# Revit family: Light_Fixture-Wall_Sconce-KOHLER-PURIST-K-27262_1
name_source: partatom
category: Lighting Fixtures
revit_build: Autodesk Revit 2017 (Build: 20160225_1515(x64)
units: mm (PartAtom-declared; Revit-internal decimal feet)

## family parameters
Cut with Voids When Loaded = No
Host = Face
Light Source = Yes
OmniClass Number = 23.35.47.00
OmniClass Title = Electrical Lighting
Part Type = Normal
Room Calculation Point = No
Round Connector Dimension = Use Diameter
Shared = No

## types (5) — shared parameters
ADA Compliant = No
Apparent Load = 0 VA
Assembly Code = D5040.50
Color Filter = 16777215
Date Modified = 04/27/2021
Default Elevation = 60"
Description = PURIST 1-LIGHT SCONCE
Dimming Lamp Color Temperature Shift = Incandescent Lamp Curve
Electrical Connector = Yes
Electrical Note = One dedicated circuit required
Emit from Line Length = 3"
Hardware Included = Yes
Height = 13 1/8"
Lamp = T10 BULB
Length = 7 1/4"
Light Source Symbol Size = 7"
Manufacturer = KOHLER Co.
Master Format 2014 = 26 51 13
Master Format 2014 Name = Interior Lighting Fixtures, Lamps, And Ballasts
Material = Premium Metal Construction
Product Documentation Link = https://www.us.kohler.com
Product Name = PURIST
Product Page URL = http://www.us.kohler.com
URL = https://www.us.kohler.com
Voltage = 120 V
WaterSense Certified = No
Width = 4 3/4"

## per-type parameters (varying)
| type | Finish | Model | Type |
| CPL-Polished Chrome | KOHLER-Metal-CPL-Polished_Chrome | K-27262-SC01-CPL | 1 |
| BNL-Brushed Nickel | KOHLER-Metal-BNL-Brushed_Nickel | K-27262-SC01-BNL | 2 |
| BLL-Matte Black | KOHLER-Metal-BLL-Matte_Black | K-27262-SC01-BLL | 3 |
| SNL-Polished Nickel | KOHLER-Metal-SNL-Polished_Nickel | K-27262-SC01-SNL | 4 |
| 2GL-Brushed Modern Brass | KOHLER-Metal-2GL-Brushed_Modern_Brass | K-27262-SC01-2GL | 5 |

## geometry (parser evidence)
native form markers: Sweep x5
no freeform markers — native parametric forms only
